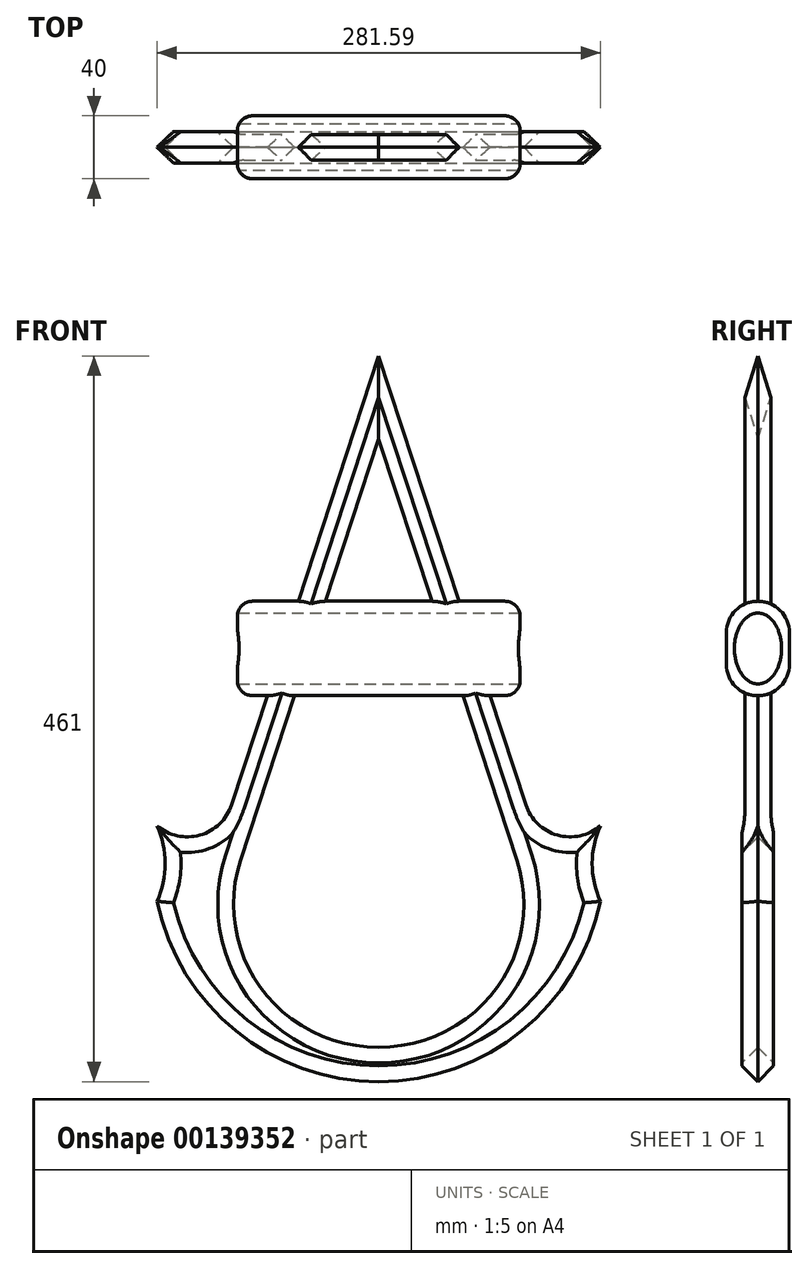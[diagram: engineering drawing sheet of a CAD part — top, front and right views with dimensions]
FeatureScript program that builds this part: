
annotation { "Feature Type Name" : "Feature", "Feature Type Description" : "" }
export const myFeature = defineFeature(function(context is Context, id is Id, definition is map)
    precondition{}
    {
        {
            var Q0;
            Q0=qCreatedBy(makeId("Front.planeOp"),FACE);
            var sketch = newSketch(context, id + "F0", { "sketchPlane" : qUnion([Q0])});
            skLineSegment(sketch, "E0", {"start": v(-112.99, 290.24) * mm, "end": v(-206.38, 5.15) * mm});
            skArc(sketch, "E1", {"start": v(-253.78, -8.17) * mm, "mid": v(-226.53, -14.16) * mm, "end": v(-206.38, 5.15) * mm});
            skArc(sketch, "E2", {"start": v(-253.78, -56.17) * mm, "mid": v(-248.58, -32.17) * mm, "end": v(-253.78, -8.17) * mm});
            skLineSegment(sketch, "E3", {"start": v(-112.99, 290.24) * mm, "end": v(-112.99, 237.57) * mm});
            skLineSegment(sketch, "E4", {"start": v(-112.99, 237.57) * mm, "end": v(-206.38, -47.52) * mm});
            skArc(sketch, "E5", {"start": v(-253.78, -56.17) * mm, "mid": v(-112.99, -170.76) * mm, "end": v(27.81, -56.17) * mm});
            skArc(sketch, "E6", {"start": v(-206.38, -47.52) * mm, "mid": v(-112.99, -148.93) * mm, "end": v(-19.6, -47.52) * mm});
            skLineSegment(sketch, "E7", {"start": v(-112.99, 237.57) * mm, "end": v(-112.99, -148.93) * mm});
            skLineSegment(sketch, "E8", {"start": v(-112.99, -148.93) * mm, "end": v(-112.99, -170.76) * mm});
            skLineSegment(sketch, "E9.MirrorCS", {"start": v(-112.99, 237.57) * mm, "end": v(-19.6, -47.52) * mm});
            skLineSegment(sketch, "E10.MirrorCS", {"start": v(-112.99, 290.24) * mm, "end": v(-19.6, 5.15) * mm});
            skArc(sketch, "E11.MirrorCS", {"start": v(27.81, -8.17) * mm, "mid": v(0.56, -14.16) * mm, "end": v(-19.6, 5.15) * mm});
            skArc(sketch, "E12.MirrorCS", {"start": v(27.81, -56.17) * mm, "mid": v(22.6, -32.17) * mm, "end": v(27.81, -8.17) * mm});
            skSolve(sketch);
        }
        {
            var Q0;
            Q0=makeQuery(id+"F0.imprint","IMPRINT",FACE,{"disambiguationData":[TD([[makeQuery(id+"F0.imprint","IMPRINT",EDGE,{"derivedFrom":sQuery(id+"F0.wireOp",EDGE,"E0")}),1.0]])]});
            var Q1;
            Q1=makeQuery(id+"F0.imprint","IMPRINT",FACE,{"disambiguationData":[TD([[makeQuery(id+"F0.imprint","IMPRINT",EDGE,{"derivedFrom":sQuery(id+"F0.wireOp",EDGE,"E3")}),1.0]])]});
            extrude(context, id + "F1", {"entities" : qUnion([Q0, Q1]), "depth" : 20 * mm});
        }
        {
            var Q0;
            Q0=makeQuery(id+"F1.opExtrude","SWEPT_EDGE",EDGE,{"disambiguationData":[OSD([sQuery(id+"F0.wireOp",EDGE,"6J5qXDiU-7dUn-nhdx-YiYW-m2wzQWXh0Yk7"),sQuery(id+"F0.wireOp",EDGE,"D04xozC7-DqkI-AIiz-Wtgi-jfPXUEKhCASJ")])]});
            var Q1;
            Q1=makeQuery(id+"F1.opExtrude","SWEPT_EDGE",EDGE,{"disambiguationData":[OSD([sQuery(id+"F0.wireOp",EDGE,"LRPx1e9p-0geG-Z7pz-MYkJ-P3BOB6wLAutz"),sQuery(id+"F0.wireOp",EDGE,"D04xozC7-DqkI-AIiz-Wtgi-jfPXUEKhCASJ")])]});
            var Q2;
            Q2=makeQuery(id+"F1.opExtrude","SWEPT_EDGE",EDGE,{"disambiguationData":[OSD([sQuery(id+"F0.wireOp",EDGE,"E4"),sQuery(id+"F0.wireOp",EDGE,"E6")])]});
            var Q3;
            Q3=makeQuery(id+"F1.opExtrude","SWEPT_EDGE",EDGE,{"disambiguationData":[OSD([sQuery(id+"F0.wireOp",EDGE,"PmAbEt39-7fAn-xuQZ-4U76-EYUopqfXnF5W"),sQuery(id+"F0.wireOp",EDGE,"E6")])]});
            fillet(context, id + "F2", {"entities" : qUnion([Q0, Q1, Q2, Q3]), "radius" : 90 * mm, "allowEdgeOverflow" : false});
        }
        {
            var Q0;
            Q0=makeQuery(id+"F1.opExtrude","CAP_EDGE",EDGE,{"disambiguationData":[OSD([sQuery(id+"F0.wireOp",EDGE,"E2")])],"isStart":false});
            var Q1;
            Q1=makeQuery(id+"F1.opExtrude","CAP_EDGE",EDGE,{"disambiguationData":[OSD([sQuery(id+"F0.wireOp",EDGE,"E6")])],"isStart":false});
            var Q2;
            Q2=makeQuery(id+"F1.opExtrude","CAP_EDGE",EDGE,{"disambiguationData":[OSD([sQuery(id+"F0.wireOp",EDGE,"E4")])],"isStart":false});
            var Q3;
            Q3=makeQuery(id+"F1.opExtrude","CAP_EDGE",EDGE,{"disambiguationData":[OSD([sQuery(id+"F0.wireOp",EDGE,"E5")])],"isStart":false});
            var Q4;
            Q4=makeQuery(id+"F1.opExtrude","CAP_EDGE",EDGE,{"disambiguationData":[OSD([sQuery(id+"F0.wireOp",EDGE,"LFlDRvoe-SYx4-lM6k-iUWW-RpskllSBHnCa")])],"isStart":false});
            var Q5;
            Q5=makeQuery(id+"F1.opExtrude","CAP_EDGE",EDGE,{"disambiguationData":[OSD([sQuery(id+"F0.wireOp",EDGE,"E1")])],"isStart":false});
            var Q6;
            Q6=makeQuery(id+"F1.opExtrude","CAP_EDGE",EDGE,{"disambiguationData":[OSD([sQuery(id+"F0.wireOp",EDGE,"PmAbEt39-7fAn-xuQZ-4U76-EYUopqfXnF5W")])],"isStart":false});
            var Q7;
            {var subQ0=sQuery(id+"F0.wireOp",EDGE,"E6");var subQ1=sQuery(id+"F0.wireOp",EDGE,"E4");Q7=makeQuery(id+"F2.opFillet","BLEND_EDGE",EDGE,{"blendedFrom":[makeQuery(id+"F1.opExtrude","SWEPT_EDGE",EDGE,{"disambiguationData":[OSD([subQ1,subQ0])]}),makeQuery(id+"F1.opExtrude","CAP_FACE",FACE,{"disambiguationData":[OSD([sQuery(id+"F0.wireOp",EDGE,"E0"),sQuery(id+"F0.wireOp",EDGE,"sThl2cjm-VwqJ-K9P4-ouzU-Yl5ci62fVaHm"),sQuery(id+"F0.wireOp",EDGE,"E1"),sQuery(id+"F0.wireOp",EDGE,"Xm765S3g-g8RI-xCbF-Oz9J-TPOFrXNZ0pQp"),sQuery(id+"F0.wireOp",EDGE,"E2"),sQuery(id+"F0.wireOp",EDGE,"LFlDRvoe-SYx4-lM6k-iUWW-RpskllSBHnCa"),subQ1,sQuery(id+"F0.wireOp",EDGE,"PmAbEt39-7fAn-xuQZ-4U76-EYUopqfXnF5W"),sQuery(id+"F0.wireOp",EDGE,"E5"),subQ0])],"isStart":false})],"blendedInto":[makeQuery(id+"F1.opExtrude","CAP_FACE",FACE,{"disambiguationData":[OSD([sQuery(id+"F0.wireOp",EDGE,"E0"),sQuery(id+"F0.wireOp",EDGE,"sThl2cjm-VwqJ-K9P4-ouzU-Yl5ci62fVaHm"),sQuery(id+"F0.wireOp",EDGE,"E1"),sQuery(id+"F0.wireOp",EDGE,"Xm765S3g-g8RI-xCbF-Oz9J-TPOFrXNZ0pQp"),sQuery(id+"F0.wireOp",EDGE,"E2"),sQuery(id+"F0.wireOp",EDGE,"LFlDRvoe-SYx4-lM6k-iUWW-RpskllSBHnCa"),subQ1,sQuery(id+"F0.wireOp",EDGE,"PmAbEt39-7fAn-xuQZ-4U76-EYUopqfXnF5W"),sQuery(id+"F0.wireOp",EDGE,"E5"),subQ0])],"isStart":false})]});}
            var Q8;
            Q8=makeQuery(id+"F1.opExtrude","CAP_EDGE",EDGE,{"disambiguationData":[OSD([sQuery(id+"F0.wireOp",EDGE,"E0")])],"isStart":false});
            var Q9;
            Q9=makeQuery(id+"F1.opExtrude","CAP_EDGE",EDGE,{"disambiguationData":[OSD([sQuery(id+"F0.wireOp",EDGE,"sThl2cjm-VwqJ-K9P4-ouzU-Yl5ci62fVaHm")])],"isStart":false});
            var Q10;
            Q10=makeQuery(id+"F1.opExtrude","CAP_EDGE",EDGE,{"disambiguationData":[OSD([sQuery(id+"F0.wireOp",EDGE,"Xm765S3g-g8RI-xCbF-Oz9J-TPOFrXNZ0pQp")])],"isStart":false});
            var Q11;
            {var subQ0=sQuery(id+"F0.wireOp",EDGE,"E6");var subQ1=sQuery(id+"F0.wireOp",EDGE,"PmAbEt39-7fAn-xuQZ-4U76-EYUopqfXnF5W");Q11=makeQuery(id+"F2.opFillet","BLEND_EDGE",EDGE,{"blendedFrom":[makeQuery(id+"F1.opExtrude","SWEPT_EDGE",EDGE,{"disambiguationData":[OSD([subQ1,subQ0])]}),makeQuery(id+"F1.opExtrude","CAP_FACE",FACE,{"disambiguationData":[OSD([sQuery(id+"F0.wireOp",EDGE,"E0"),sQuery(id+"F0.wireOp",EDGE,"sThl2cjm-VwqJ-K9P4-ouzU-Yl5ci62fVaHm"),sQuery(id+"F0.wireOp",EDGE,"E1"),sQuery(id+"F0.wireOp",EDGE,"Xm765S3g-g8RI-xCbF-Oz9J-TPOFrXNZ0pQp"),sQuery(id+"F0.wireOp",EDGE,"E2"),sQuery(id+"F0.wireOp",EDGE,"LFlDRvoe-SYx4-lM6k-iUWW-RpskllSBHnCa"),sQuery(id+"F0.wireOp",EDGE,"E4"),subQ1,sQuery(id+"F0.wireOp",EDGE,"E5"),subQ0])],"isStart":false})],"blendedInto":[makeQuery(id+"F1.opExtrude","CAP_FACE",FACE,{"disambiguationData":[OSD([sQuery(id+"F0.wireOp",EDGE,"E0"),sQuery(id+"F0.wireOp",EDGE,"sThl2cjm-VwqJ-K9P4-ouzU-Yl5ci62fVaHm"),sQuery(id+"F0.wireOp",EDGE,"E1"),sQuery(id+"F0.wireOp",EDGE,"Xm765S3g-g8RI-xCbF-Oz9J-TPOFrXNZ0pQp"),sQuery(id+"F0.wireOp",EDGE,"E2"),sQuery(id+"F0.wireOp",EDGE,"LFlDRvoe-SYx4-lM6k-iUWW-RpskllSBHnCa"),sQuery(id+"F0.wireOp",EDGE,"E4"),subQ1,sQuery(id+"F0.wireOp",EDGE,"E5"),subQ0])],"isStart":false})]});}
            var Q12;
            {var subQ0=sQuery(id+"F0.wireOp",EDGE,"E6");var subQ1=sQuery(id+"F0.wireOp",EDGE,"E4");Q12=makeQuery(id+"F2.opFillet","BLEND_EDGE",EDGE,{"blendedFrom":[makeQuery(id+"F1.opExtrude","SWEPT_EDGE",EDGE,{"disambiguationData":[OSD([subQ1,subQ0])]}),makeQuery(id+"F1.opExtrude","CAP_FACE",FACE,{"disambiguationData":[OSD([sQuery(id+"F0.wireOp",EDGE,"E0"),sQuery(id+"F0.wireOp",EDGE,"sThl2cjm-VwqJ-K9P4-ouzU-Yl5ci62fVaHm"),sQuery(id+"F0.wireOp",EDGE,"E1"),sQuery(id+"F0.wireOp",EDGE,"Xm765S3g-g8RI-xCbF-Oz9J-TPOFrXNZ0pQp"),sQuery(id+"F0.wireOp",EDGE,"E2"),sQuery(id+"F0.wireOp",EDGE,"LFlDRvoe-SYx4-lM6k-iUWW-RpskllSBHnCa"),subQ1,sQuery(id+"F0.wireOp",EDGE,"PmAbEt39-7fAn-xuQZ-4U76-EYUopqfXnF5W"),sQuery(id+"F0.wireOp",EDGE,"E5"),subQ0])],"isStart":true})],"blendedInto":[makeQuery(id+"F1.opExtrude","CAP_FACE",FACE,{"disambiguationData":[OSD([sQuery(id+"F0.wireOp",EDGE,"E0"),sQuery(id+"F0.wireOp",EDGE,"sThl2cjm-VwqJ-K9P4-ouzU-Yl5ci62fVaHm"),sQuery(id+"F0.wireOp",EDGE,"E1"),sQuery(id+"F0.wireOp",EDGE,"Xm765S3g-g8RI-xCbF-Oz9J-TPOFrXNZ0pQp"),sQuery(id+"F0.wireOp",EDGE,"E2"),sQuery(id+"F0.wireOp",EDGE,"LFlDRvoe-SYx4-lM6k-iUWW-RpskllSBHnCa"),subQ1,sQuery(id+"F0.wireOp",EDGE,"PmAbEt39-7fAn-xuQZ-4U76-EYUopqfXnF5W"),sQuery(id+"F0.wireOp",EDGE,"E5"),subQ0])],"isStart":true})]});}
            var Q13;
            Q13=makeQuery(id+"F1.opExtrude","CAP_EDGE",EDGE,{"disambiguationData":[OSD([sQuery(id+"F0.wireOp",EDGE,"E5")])],"isStart":true});
            var Q14;
            Q14=makeQuery(id+"F1.opExtrude","CAP_EDGE",EDGE,{"disambiguationData":[OSD([sQuery(id+"F0.wireOp",EDGE,"sThl2cjm-VwqJ-K9P4-ouzU-Yl5ci62fVaHm")])],"isStart":true});
            var Q15;
            Q15=makeQuery(id+"F1.opExtrude","CAP_EDGE",EDGE,{"disambiguationData":[OSD([sQuery(id+"F0.wireOp",EDGE,"E0")])],"isStart":true});
            var Q16;
            Q16=makeQuery(id+"F1.opExtrude","CAP_EDGE",EDGE,{"disambiguationData":[OSD([sQuery(id+"F0.wireOp",EDGE,"E4")])],"isStart":true});
            var Q17;
            Q17=makeQuery(id+"F1.opExtrude","CAP_EDGE",EDGE,{"disambiguationData":[OSD([sQuery(id+"F0.wireOp",EDGE,"PmAbEt39-7fAn-xuQZ-4U76-EYUopqfXnF5W")])],"isStart":true});
            var Q18;
            Q18=makeQuery(id+"F1.opExtrude","CAP_EDGE",EDGE,{"disambiguationData":[OSD([sQuery(id+"F0.wireOp",EDGE,"E2")])],"isStart":true});
            var Q19;
            Q19=makeQuery(id+"F1.opExtrude","CAP_EDGE",EDGE,{"disambiguationData":[OSD([sQuery(id+"F0.wireOp",EDGE,"E6")])],"isStart":true});
            var Q20;
            Q20=makeQuery(id+"F1.opExtrude","CAP_EDGE",EDGE,{"disambiguationData":[OSD([sQuery(id+"F0.wireOp",EDGE,"LFlDRvoe-SYx4-lM6k-iUWW-RpskllSBHnCa")])],"isStart":true});
            var Q21;
            Q21=makeQuery(id+"F1.opExtrude","CAP_EDGE",EDGE,{"disambiguationData":[OSD([sQuery(id+"F0.wireOp",EDGE,"Xm765S3g-g8RI-xCbF-Oz9J-TPOFrXNZ0pQp")])],"isStart":true});
            var Q22;
            Q22=makeQuery(id+"F1.opExtrude","CAP_EDGE",EDGE,{"disambiguationData":[OSD([sQuery(id+"F0.wireOp",EDGE,"E1")])],"isStart":true});
            var Q23;
            {var subQ0=sQuery(id+"F0.wireOp",EDGE,"E6");var subQ1=sQuery(id+"F0.wireOp",EDGE,"PmAbEt39-7fAn-xuQZ-4U76-EYUopqfXnF5W");Q23=makeQuery(id+"F2.opFillet","BLEND_EDGE",EDGE,{"blendedFrom":[makeQuery(id+"F1.opExtrude","SWEPT_EDGE",EDGE,{"disambiguationData":[OSD([subQ1,subQ0])]}),makeQuery(id+"F1.opExtrude","CAP_FACE",FACE,{"disambiguationData":[OSD([sQuery(id+"F0.wireOp",EDGE,"E0"),sQuery(id+"F0.wireOp",EDGE,"sThl2cjm-VwqJ-K9P4-ouzU-Yl5ci62fVaHm"),sQuery(id+"F0.wireOp",EDGE,"E1"),sQuery(id+"F0.wireOp",EDGE,"Xm765S3g-g8RI-xCbF-Oz9J-TPOFrXNZ0pQp"),sQuery(id+"F0.wireOp",EDGE,"E2"),sQuery(id+"F0.wireOp",EDGE,"LFlDRvoe-SYx4-lM6k-iUWW-RpskllSBHnCa"),sQuery(id+"F0.wireOp",EDGE,"E4"),subQ1,sQuery(id+"F0.wireOp",EDGE,"E5"),subQ0])],"isStart":true})],"blendedInto":[makeQuery(id+"F1.opExtrude","CAP_FACE",FACE,{"disambiguationData":[OSD([sQuery(id+"F0.wireOp",EDGE,"E0"),sQuery(id+"F0.wireOp",EDGE,"sThl2cjm-VwqJ-K9P4-ouzU-Yl5ci62fVaHm"),sQuery(id+"F0.wireOp",EDGE,"E1"),sQuery(id+"F0.wireOp",EDGE,"Xm765S3g-g8RI-xCbF-Oz9J-TPOFrXNZ0pQp"),sQuery(id+"F0.wireOp",EDGE,"E2"),sQuery(id+"F0.wireOp",EDGE,"LFlDRvoe-SYx4-lM6k-iUWW-RpskllSBHnCa"),sQuery(id+"F0.wireOp",EDGE,"E4"),subQ1,sQuery(id+"F0.wireOp",EDGE,"E5"),subQ0])],"isStart":true})]});}
            var Q24;
            Q24=makeQuery(id+"F1.opExtrude","CAP_EDGE",EDGE,{"disambiguationData":[OSD([sQuery(id+"F0.wireOp",EDGE,"E11.MirrorCS")])],"isStart":false});
            var Q25;
            Q25=makeQuery(id+"F1.opExtrude","CAP_EDGE",EDGE,{"disambiguationData":[OSD([sQuery(id+"F0.wireOp",EDGE,"E12.MirrorCS")])],"isStart":false});
            var Q26;
            Q26=makeQuery(id+"F1.opExtrude","CAP_EDGE",EDGE,{"disambiguationData":[OSD([sQuery(id+"F0.wireOp",EDGE,"E10.MirrorCS")])],"isStart":true});
            var Q27;
            Q27=makeQuery(id+"F1.opExtrude","CAP_EDGE",EDGE,{"disambiguationData":[OSD([sQuery(id+"F0.wireOp",EDGE,"E11.MirrorCS")])],"isStart":true});
            var Q28;
            Q28=makeQuery(id+"F1.opExtrude","CAP_EDGE",EDGE,{"disambiguationData":[OSD([sQuery(id+"F0.wireOp",EDGE,"E12.MirrorCS")])],"isStart":true});
            chamfer(context, id + "F3", {"entities" : qUnion([Q0, Q1, Q2, Q3, Q4, Q5, Q6, Q7, Q8, Q9, Q10, Q11, Q12, Q13, Q14, Q15, Q16, Q17, Q18, Q19, Q20, Q21, Q22, Q23, Q24, Q25, Q26, Q27, Q28]), "width" : 10 * mm, "tangentPropagation" : true});
        }
        {
            var Q0;
            Q0=qCreatedBy(makeId("Front.planeOp"),FACE);
            cPlane(context, id + "F4", {"entities" : qUnion([Q0]), "cplaneType" : CPlaneType.OFFSET, "offset" : 10 * mm, "oppositeDirection" : true, "width" : 150 * mm, "height" : 150 * mm});
        }
        {
            var Q0;
            Q0=qCreatedBy(id+"F4.planeOp",FACE);
            var sketch = newSketch(context, id + "F5", { "sketchPlane" : qUnion([Q0])});
            skLineSegment(sketch, "E13", {"start": v(-112.99, -136.1) * mm, "end": v(-112.99, 263.9) * mm});
            skLineSegment(sketch, "E14.bottom", {"start": v(-112.99, 134.4) * mm, "end": v(-202.99, 134.4) * mm});
            skLineSegment(sketch, "E14.top", {"start": v(-112.99, 74.4) * mm, "end": v(-202.99, 74.4) * mm});
            skLineSegment(sketch, "E14.left", {"start": v(-112.99, 134.4) * mm, "end": v(-112.99, 74.4) * mm});
            skLineSegment(sketch, "E14.right", {"start": v(-202.99, 134.4) * mm, "end": v(-202.99, 74.4) * mm});
            skLineSegment(sketch, "E15.MirrorCS", {"start": v(-22.99, 134.4) * mm, "end": v(-22.99, 74.4) * mm});
            skLineSegment(sketch, "E16.MirrorCS", {"start": v(-112.99, 74.4) * mm, "end": v(-22.99, 74.4) * mm});
            skLineSegment(sketch, "E17.MirrorCS", {"start": v(-112.99, 134.4) * mm, "end": v(-22.99, 134.4) * mm});
            skSolve(sketch);
        }
        {
            var Q0;
            Q0=makeQuery(id+"F5.imprint","IMPRINT",FACE,{"disambiguationData":[TD([[makeQuery(id+"F5.imprint","IMPRINT",EDGE,{"derivedFrom":sQuery(id+"F5.wireOp",EDGE,"E15.MirrorCS")}),-1.0]])]});
            var Q1;
            Q1=makeQuery(id+"F5.imprint","IMPRINT",FACE,{"disambiguationData":[TD([[makeQuery(id+"F5.imprint","IMPRINT",EDGE,{"derivedFrom":sQuery(id+"F5.wireOp",EDGE,"E14.bottom")}),1.0]])]});
            extrude(context, id + "F6", {"entities" : qUnion([Q0, Q1]), "operationType" : NewBodyOperationType.ADD, "depth" : 40 * mm});
        }
        {
            var Q0;
            Q0=makeQuery(id+"F6.opExtrude","CAP_EDGE",EDGE,{"disambiguationData":[OSD([sQuery(id+"F5.wireOp",EDGE,"E14.top"),sQuery(id+"F5.wireOp",EDGE,"E16.MirrorCS")])],"isStart":false});
            var Q1;
            Q1=makeQuery(id+"F6.opExtrude","CAP_EDGE",EDGE,{"disambiguationData":[OSD([sQuery(id+"F5.wireOp",EDGE,"E14.top"),sQuery(id+"F5.wireOp",EDGE,"E16.MirrorCS")])],"isStart":true});
            var Q2;
            Q2=makeQuery(id+"F6.opExtrude","CAP_EDGE",EDGE,{"disambiguationData":[OSD([sQuery(id+"F5.wireOp",EDGE,"E14.bottom"),sQuery(id+"F5.wireOp",EDGE,"E17.MirrorCS")])],"isStart":false});
            var Q3;
            Q3=makeQuery(id+"F6.opExtrude","CAP_EDGE",EDGE,{"disambiguationData":[OSD([sQuery(id+"F5.wireOp",EDGE,"E14.bottom"),sQuery(id+"F5.wireOp",EDGE,"E17.MirrorCS")])],"isStart":true});
            fillet(context, id + "F7", {"entities" : qUnion([Q0, Q1, Q2, Q3]), "radius" : 19.9 * mm, "tangentPropagation" : true, "allowEdgeOverflow" : false});
        }
        {
            var Q0;
            Q0=makeQuery(id+"F6.opExtrude","SWEPT_FACE",FACE,{"disambiguationData":[OSD([sQuery(id+"F5.wireOp",EDGE,"E15.MirrorCS")])]});
            var sketch = newSketch(context, id + "F8", { "sketchPlane" : qUnion([Q0])});
            skLineSegment(sketch, "E18", {"start": v(-9.9, 134.4) * mm, "end": v(-9.9, 74.4) * mm});
            skEllipse(sketch, "E19", {"center": v(-9.9, 104.4) * mm, "majorRadius": 22.5 * mm, "minorRadius": 15 * mm, "majorAxis": v(0, 1)});
            skPoint(sketch, "E20", {"position": v(-9.9, 126.9) * mm});
            skPoint(sketch, "E21", {"position": v(-9.9, 81.9) * mm});
            skLineSegment(sketch, "E22", {"start": v(-9.9, 104.4) * mm, "end": v(5.1, 104.4) * mm});
            skSolve(sketch);
        }
        {
            var Q0;
            {var subQ0=sQuery(id+"F8.wireOp",EDGE,"E18");var subQ1=makeQuery(id+"F8.imprint","INTERSECT",VERTEX,{"derivedFrom":[subQ0,sQuery(id+"F8.wireOp",EDGE,"E22")]});Q0=makeQuery(id+"F8.imprint","IMPRINT",FACE,{"disambiguationData":[TD([[makeQuery(id+"F8.imprint","IMPRINT",EDGE,{"disambiguationData":[TD([[subQ1,1.0]])],"derivedFrom":subQ0}),-1.0]])]});}
            var Q1;
            {var subQ0=sQuery(id+"F8.wireOp",EDGE,"E22");Q1=makeQuery(id+"F8.imprint","IMPRINT",FACE,{"disambiguationData":[TD([[makeQuery(id+"F8.imprint","IMPRINT",EDGE,{"derivedFrom":subQ0}),1.0]])]});}
            var Q2;
            {var subQ0=sQuery(id+"F8.wireOp",EDGE,"E22");Q2=makeQuery(id+"F8.imprint","IMPRINT",FACE,{"disambiguationData":[TD([[makeQuery(id+"F8.imprint","IMPRINT",EDGE,{"derivedFrom":subQ0}),-1.0]])]});}
            extrude(context, id + "F9", {"entities" : qUnion([Q0, Q1, Q2]), "operationType" : NewBodyOperationType.REMOVE, "endBound" : BoundingType.THROUGH_ALL, "oppositeDirection" : true, "depth" : 25 * mm});
        }
        {
            var Q0;
            Q0=makeQuery(id+"F6.opExtrude","CAP_EDGE",EDGE,{"disambiguationData":[OSD([sQuery(id+"F5.wireOp",EDGE,"E15.MirrorCS")])],"isStart":false});
            var Q1;
            Q1=makeQuery(id+"F6.opExtrude","CAP_EDGE",EDGE,{"disambiguationData":[OSD([sQuery(id+"F5.wireOp",EDGE,"E14.right")])],"isStart":false});
            fillet(context, id + "F10", {"entities" : qUnion([Q0, Q1]), "radius" : 10 * mm, "tangentPropagation" : true, "allowEdgeOverflow" : false});
        }
    });
